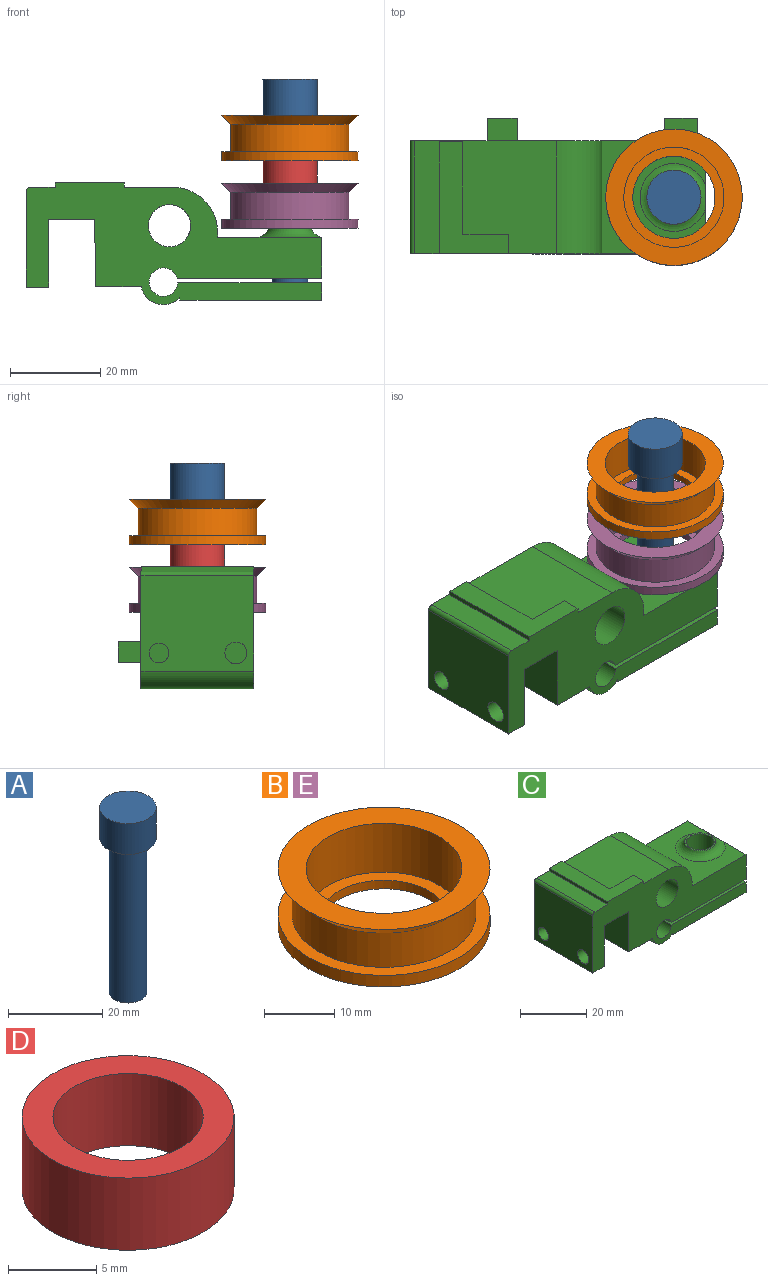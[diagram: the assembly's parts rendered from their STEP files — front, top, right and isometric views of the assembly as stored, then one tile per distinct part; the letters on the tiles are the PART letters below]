
ASSEMBLY  parts=5 mates=4
PART A: 5 faces, bbox 12x12x48 mm
  f0: cylinder r=4mm len=40mm, axis (0,0,-1), area 1005.3mm2, adj f1,f4
  f1: plane 8x8mm, normal (0,0,-1), area 50.3mm2, adj f0
  f2: cylinder r=6mm len=12mm, axis (0,0,-1), area 301.6mm2, adj f3,f4
  f3: plane 12x12mm, normal (0,0,1), area 113.1mm2, adj f2
  f4: plane 12x12mm, normal (0,0,-1), area 62.8mm2, adj f0,f2
PART B: 9 faces, bbox 30.2x30.2x10 mm
  f0: plane 30.2x30.2mm, normal (0,0,1), area 329.2mm2, adj f1,f8
  f1: cylinder r=11.1mm len=22.2mm, axis (0,0,-1), area 592.8mm2, adj f0,f2
  f2: plane 22.2x22.2mm, normal (0,0,1), area 126.9mm2, adj f1,f3
  f3: cylinder r=9.1mm len=18.2mm, axis (0,0,-1), area 85.8mm2, adj f2,f4
  f4: plane 30.2x30.2mm, normal (0,0,-1), area 456.2mm2, adj f3,f5
  f5: cylinder r=15.1mm len=30.2mm, axis (0,0,-1), area 189.8mm2, adj f4,f6
  f6: plane 30.2x30.2mm, normal (0,0,1), area 177.2mm2, adj f5,f7
  f7: cylinder r=13.1mm len=26.2mm, axis (0,0,-1), area 493.9mm2, adj f6,f8
  f8: cone r=15.1mm half-angle=45deg, axis (0,0,1), area 250.6mm2, adj f0,f7
PART C: 43 faces, bbox 68.9x30x27 mm
  f0: plane 25x3.86mm, normal (1,0,0), area 96.5mm2, adj f4,f14,f15,f19
  f1: cylinder r=4.17mm len=8.35mm, axis (0,0,1), area 101.3mm2, adj f4,f19
  f2: plane 25x10.1mm, normal (0,0,-1), area 252.6mm2, adj f13,f14,f15,f17
  f3: plane 25x0.6mm, normal (-1,0,0), area 14.9mm2, adj f4,f14,f15,f17
  f4: plane 31.35x25mm, normal (0,0,-1), area 729mm2, adj f0,f1,f3,f14,f15
  f5: plane 25x9.08mm, normal (1,0,0), area 226.1mm2, adj f6,f14,f15,f20,f24
  f6: plane 25x23mm, normal (0,0,1), area 400mm2, adj f5,f7,f14,f15,f24
  f7: plane 25x1.1mm, normal (1,0,0), area 27.5mm2, adj f6,f14,f15,f25
  f8: plane 31.42x25mm, normal (0,0,1), area 611.6mm2, adj f14,f15,f25,f27,f37,f38,f39,f40
  f9: plane 25x21.09mm, normal (-1,0,0), area 493.5mm2, adj f10,f14,f15,f22,f23,f27
  f10: plane 25x5mm, normal (0,0,-1), area 125mm2, adj f9,f11,f14,f15
  f11: plane 25x15mm, normal (1,0,0), area 341.3mm2, adj f10,f12,f14,f15,f22,f23
  f12: plane 25x10.2mm, normal (0,0,-1), area 255mm2, adj f11,f13,f14,f15
  f13: plane 25x14.91mm, normal (-1,0,-0.01), area 372.8mm2, adj f2,f12,f14,f15
  f14: plane 65.42x27mm, normal (0,-1,0), area 1014.1mm2, adj f0,f2,f3,f4,f5,f6,f7,f8
  f15: plane 65.42x26mm, normal (0,1,0), area 938.8mm2, adj f0,f2,f3,f4,f5,f6,f7,f8
  f16: cylinder r=4.17mm len=11.04mm, axis (0,0,1), area 289.6mm2, adj f20,f21
  f17: cylinder r=5mm len=25mm, axis (0,-1,0), area 273.8mm2, adj f2,f3,f14,f15
  f18: cylinder r=3.15mm len=25mm, axis (0,-1,0), area 469.5mm2, adj f14,f15,f19,f20
  f19: plane 31.86x25mm, normal (0,0,1), area 741.8mm2, adj f0,f1,f14,f15,f18
  f20: plane 31.98x30mm, normal (0,0,-1), area 781.2mm2, adj f5,f14,f15,f16,f18,f29,f30,f31
  f21: plane 9.35x9.35mm, normal (0,0,1), area 13.9mm2, adj f16,f24
  f22: cylinder r=2.43mm len=5mm, axis (-1,0,0), area 76.2mm2, adj f9,f11
  f23: cylinder r=2.2mm len=5mm, axis (-1,0,0), area 69.1mm2, adj f9,f11
  f24: torus R=7.5mm, axis (0,0,-1), area 134.6mm2, adj f5,f6,f21
  f25: cylinder r=10mm len=25mm, axis (0,-1,0), area 392.7mm2, adj f7,f8,f14,f15
  f26: cylinder r=4.68mm len=25mm, axis (0,-1,0), area 735.2mm2, adj f14,f15
  f27: cylinder r=1mm len=25mm, axis (0,-1,0), area 39.3mm2, adj f8,f9,f14,f15
  f28: plane 7.3x5mm, normal (0,0,1), area 36.5mm2, adj f15,f29,f30,f31
  f29: plane 5x4.12mm, normal (1,0,0), area 20.6mm2, adj f15,f20,f28,f31
  f30: plane 5x4.12mm, normal (-1,0,0), area 20.6mm2, adj f15,f20,f28,f31
  f31: plane 7.3x4.12mm, normal (0,1,0), area 30.1mm2, adj f20,f28,f29,f30
  f32: plane 6.63x5mm, normal (0,0,1), area 33.2mm2, adj f15,f33,f35,f36
  f33: plane 5x4.5mm, normal (1,0,0), area 22.5mm2, adj f15,f32,f34,f36
  f34: plane 6.63x5mm, normal (0,0,-1), area 33.2mm2, adj f15,f33,f35,f36
  f35: plane 5x4.5mm, normal (-1,0,0), area 22.5mm2, adj f15,f32,f34,f36
  f36: plane 6.63x4.5mm, normal (0,1,0), area 29.9mm2, adj f32,f33,f34,f35
  f37: plane 24.79x1mm, normal (-1,0,0), area 24.8mm2, adj f8,f14,f41,f42
  f38: plane 4.34x1mm, normal (1,0,0), area 4.3mm2, adj f8,f14,f39,f42
  f39: plane 10.05x1mm, normal (0,1,0), area 10.1mm2, adj f8,f38,f40,f42
  f40: plane 20.45x1mm, normal (1,0,0), area 20.4mm2, adj f8,f39,f41,f42
  f41: plane 5.26x1mm, normal (0,1,0), area 5.3mm2, adj f8,f37,f40,f42
  f42: plane 24.79x15.31mm, normal (0,0,1), area 174mm2, adj f14,f37,f38,f39,f40,f41
PART D: 4 faces, bbox 12x12x5 mm
  f0: cylinder r=4.25mm len=8.5mm, axis (0,0,-1), area 133.5mm2, adj f2,f3
  f1: cylinder r=6mm len=12mm, axis (0,0,-1), area 188.5mm2, adj f2,f3
  f2: plane 12x12mm, normal (0,0,1), area 56.4mm2, adj f0,f1
  f3: plane 12x12mm, normal (0,0,-1), area 56.4mm2, adj f0,f1
PART E: same geometry as B
PLACE A t=(23.78,-12.5,-2.1)mm
PLACE B t=(23.78,-12.5,33.1)mm
PLACE C at identity
PLACE D rot(axis=(1,0,0),180deg) t=(23.78,-12.5,27.9)mm
PLACE E t=(23.78,-12.5,18.1)mm
MATE fastened D.f0 <-> E.f1  axis (0,0,1) through (23.78,-12.5,22.9)mm
MATE fastened A.f0 <-> B.f1  axis (0,0,-1) through (23.78,-12.5,37.9)mm
MATE fastened B.f1 <-> E.f1  axis (0,0,-1) through (23.78,-12.5,27.9)mm
MATE fastened E.f1 <-> C.f1  axis (0,0,-1) through (23.78,-12.5,12.9)mm
